# Revit family: Geryon SRD-E01
name_source: partatom
category: Türen
revit_build: Autodesk Revit 2016 (Build: 20150220_1215(x64)
units: mm (PartAtom-declared; Revit-internal decimal feet)

## family parameters
Beim Laden mit Abzugskörper schneiden = Nein
Gemeinsam genutzt = Nein
Immer vertikal = Ja
OmniClass-Nummer = 23.30.10.00
OmniClass-Titel = Doors
Raumberechnungspunkt = Nein

## types (8) — shared parameters
Analytische Konstruktion = <Keine Auswahl>
CoverMaterial = Glas
Date of publishing = 1/16/2017
Design country = Germany
Dicke = 63 mm  [stored 0.206693 ft]
Edition number = 1
ElementWeight = 0.00 kg
FrameMaterial = 1.4401 - A4
Funktion = Außen
HasLockInside = Nein
HasLockInside 120 = Nein
HasLockInside 180 = Nein
HasShellTopFrame = Ja
HasShutOffDevice = Nein
HasShutOffDeviceInside = Nein
HasShutOffDeviceInside120 = Nein
HasShutOffDeviceInside180 = Nein
Hersteller = Kaba GmbH
Konstruktionstyp = Revolving Door
Manufacturer = Kaba GmbH
Manufacturer country = Germany
Manufacturer name = DORMA
Material main = Metal
Material secondary = Glass
Modell = Talos RDR-E01
Nominal height = 2300
OperatingWeight = 0.00 kg
Product SKU = Geryon_SRD-E01
RubberMaterial = Zellkautschuk - EPDM
SectionWidth = 4300 mm
Technical description = http://www.kaba.com
Type = Geryon SRD-E01
URL = http://www.kaba.com
Weight = 0.00 kg
zero-valued in all types: Nominal width

## per-type parameters (varying)
- SRD-E01 1500: AccessLengthOrRadius=780 mm; BaseType=139; ClearHeight=2700 mm; ConsoleS1=831 mm; ConsoleS2=831 mm; ConsoleType=console : Type 5; CoverWidth=200 mm  [stored 0.656168 ft]; Diameter=810 mm; DiameterCoverFront=890 mm  [stored 2.91995 ft]; DiameterGlassInside=789 mm; DiameterGlassOutside=801 mm; DiameterNightLock=840 mm  [stored 2.75591 ft]; DiameterNightLockCover=870 mm; DiameterNightLockFrame=831 mm; DiameterNightLockGlassInside=849 mm  [stored 2.78543 ft]; DiameterNightLockGlassOutside=860 mm; DoorThickness=40 mm  [stored 0.131234 ft]; DoorWidth=740 mm; FrameThickness=63 mm  [stored 0.206693 ft]; FrameThicknessCenter=75 mm; GasShellTopFrame 120=Nein; HandleMaterial=1.4401 - A4; HasCentralColumn=Ja; HasCentralColumn 120=Nein; HasCentralColumn 180=Ja; HasConsoleS1=Ja; HasConsoleS1 120=Nein; HasConsoleS1 180=Ja; HasConsoleS2=Ja; HasConsoleS2 120=Nein; HasConsoleS2 180=Ja; HasGrabHandles=Nein; HasGrabHandles 120=Nein; HasGrabHandles 180=Ja; HasHandleBar=Ja; HasLock=Nein; HasLock 120=Nein; HasLock 180=Nein; HasShellTopFrame 180=Ja; Height=2900 mm; MotorDriveType=K8-SA2; OuterDiameter=2000 mm; ProfileCenter=0 mm  [stored 0 ft]; ProfileWidth=40 mm  [stored 0.131234 ft]; RotationInterval 120=Nein; RotationInterval 180=Ja; StandardUsed=3; Width=1600 mm
- SRD-E01 1700: AccessLengthOrRadius=880 mm; BaseType=109 mm; ClearHeight=2600 mm; ConsoleS1=931 mm; ConsoleS2=931 mm; ConsoleType=console : Type 4; CoverWidth=300 mm; Diameter=910 mm  [stored 2.98556 ft]; DiameterCoverFront=990 mm  [stored 3.24803 ft]; DiameterGlassInside=889 mm; DiameterGlassOutside=901 mm; DiameterNightLock=940 mm; DiameterNightLockCover=970 mm; DiameterNightLockFrame=931 mm; DiameterNightLockGlassInside=949 mm  [stored 3.11352 ft]; DiameterNightLockGlassOutside=960 mm; DoorThickness=25 mm  [stored 0.082021 ft]; DoorWidth=840 mm  [stored 2.75591 ft]; FrameThickness=35 mm  [stored 0.114829 ft]; FrameThicknessCenter=47 mm; GasShellTopFrame 120=Ja; HandleMaterial=1.4401 - A4; HasCentralColumn=Nein; HasCentralColumn 120=Nein; HasCentralColumn 180=Nein; HasConsoleS1=Ja; HasConsoleS1 120=Ja; HasConsoleS1 180=Nein; HasConsoleS2=Ja; HasConsoleS2 120=Ja; HasConsoleS2 180=Nein; HasGrabHandles=Ja; HasGrabHandles 120=Ja; HasGrabHandles 180=Nein; HasHandleBar=Nein; HasLock=Nein; HasLock 120=Nein; HasLock 180=Nein; HasShellTopFrame 180=Nein; Height=2900 mm; MotorDriveType=K8-SA1; OuterDiameter=1800 mm; ProfileCenter=7.5 mm; ProfileWidth=40 mm  [stored 0.131234 ft]; RotationInterval 120=Ja; RotationInterval 180=Nein; StandardUsed=2; Width=1800 mm
- SRD-E01 2900: AccessLengthOrRadius=1480 mm; BaseType=150; ClearHeight=2100 mm; ConsoleS1=1531 mm; ConsoleS2=1531 mm; ConsoleType=console : Type 4; CoverWidth=200 mm  [stored 0.656168 ft]; Diameter=1510 mm; DiameterCoverFront=1590 mm; DiameterGlassInside=1489 mm; DiameterGlassOutside=1501 mm; DiameterNightLock=1540 mm; DiameterNightLockCover=1570 mm; DiameterNightLockFrame=1531 mm; DiameterNightLockGlassInside=1549 mm; DiameterNightLockGlassOutside=1560 mm; DoorThickness=56 mm  [stored 0.183727 ft]; DoorWidth=1440 mm; FrameThickness=80 mm  [stored 0.262467 ft]; FrameThicknessCenter=92 mm  [stored 0.301837 ft]; GasShellTopFrame 120=Nein; HandleMaterial=1.4401 - A4; HasCentralColumn=Nein; HasCentralColumn 120=Nein; HasCentralColumn 180=Nein; HasConsoleS1=Nein; HasConsoleS1 120=Nein; HasConsoleS1 180=Nein; HasConsoleS2=Nein; HasConsoleS2 120=Nein; HasConsoleS2 180=Nein; HasGrabHandles=Nein; HasGrabHandles 120=Nein; HasGrabHandles 180=Ja; HasHandleBar=Ja; HasLock=Nein; HasLock 120=Nein; HasLock 180=Nein; HasShellTopFrame 180=Ja; Height=2300 mm; OuterDiameter=3000 mm; ProfileCenter=0 mm  [stored 0 ft]; ProfileWidth=56 mm  [stored 0.183727 ft]; RotationInterval 120=Nein; RotationInterval 180=Ja; StandardUsed=8; Width=3000 mm
- SRD-E01 1900: AccessLengthOrRadius=980 mm; BaseType=139; ClearHeight=2700 mm; ConsoleS1=1031 mm; ConsoleS2=1031 mm; ConsoleType=console : Type 5; CoverWidth=200 mm  [stored 0.656168 ft]; Diameter=1010 mm; DiameterCoverFront=1090 mm; DiameterGlassInside=989 mm; DiameterGlassOutside=1001 mm; DiameterNightLock=1040 mm; DiameterNightLockCover=1070 mm; DiameterNightLockFrame=1031 mm; DiameterNightLockGlassInside=1049 mm; DiameterNightLockGlassOutside=1060 mm; DoorThickness=40 mm  [stored 0.131234 ft]; DoorWidth=940 mm; FrameThickness=63 mm  [stored 0.206693 ft]; FrameThicknessCenter=75 mm; GasShellTopFrame 120=Nein; HandleMaterial=1.4401 - A4; HasCentralColumn=Ja; HasCentralColumn 120=Nein; HasCentralColumn 180=Ja; HasConsoleS1=Ja; HasConsoleS1 120=Nein; HasConsoleS1 180=Ja; HasConsoleS2=Ja; HasConsoleS2 120=Nein; HasConsoleS2 180=Ja; HasGrabHandles=Nein; HasGrabHandles 120=Nein; HasGrabHandles 180=Ja; HasHandleBar=Ja; HasLock=Nein; HasLock 120=Nein; HasLock 180=Nein; HasShellTopFrame 180=Ja; Height=2900 mm; MotorDriveType=K8-SA2; OuterDiameter=2000 mm; ProfileCenter=0 mm  [stored 0 ft]; ProfileWidth=40 mm  [stored 0.131234 ft]; RotationInterval 120=Nein; RotationInterval 180=Ja; StandardUsed=3; Width=2000 mm
- SRD-E01 2100: AccessLengthOrRadius=1080 mm; BaseType=220; ClearHeight=2400 mm; ConsoleS1=1131 mm; ConsoleS2=1131 mm; ConsoleType=console : Type 5; CoverWidth=300 mm; Diameter=1110 mm; DiameterCoverFront=1190 mm; DiameterGlassInside=1089 mm; DiameterGlassOutside=1101 mm; DiameterNightLock=1140 mm; DiameterNightLockCover=1170 mm; DiameterNightLockFrame=1131 mm; DiameterNightLockGlassInside=1149 mm; DiameterNightLockGlassOutside=1160 mm; DoorThickness=25 mm  [stored 0.082021 ft]; DoorWidth=1040 mm; FrameThickness=49 mm  [stored 0.160761 ft]; FrameThicknessCenter=61 mm; GasShellTopFrame 120=Nein; HandleMaterial=1.4401 - A4; HasCentralColumn=Ja; HasCentralColumn 120=Nein; HasCentralColumn 180=Ja; HasConsoleS1=Nein; HasConsoleS1 120=Nein; HasConsoleS1 180=Nein; HasConsoleS2=Nein; HasConsoleS2 120=Nein; HasConsoleS2 180=Nein; HasGrabHandles=Nein; HasGrabHandles 120=Nein; HasGrabHandles 180=Ja; HasHandleBar=Ja; HasLock=Nein; HasLock 120=Nein; HasLock 180=Nein; HasShellTopFrame 180=Ja; Height=2700 mm; MotorDriveType=K8-SA1; OuterDiameter=2200 mm; ProfileCenter=7.5 mm; ProfileWidth=40 mm  [stored 0.131234 ft]; RotationInterval 120=Nein; RotationInterval 180=Ja; StandardUsed=4; Width=2200 mm
- SRD-E01 2300: AccessLengthOrRadius=1180 mm; BaseType=220; ClearHeight=2100 mm; ConsoleS1=1231 mm; ConsoleS2=1279 mm; ConsoleType=console : Type 5; CoverWidth=200 mm  [stored 0.656168 ft]; Diameter=1210 mm; DiameterCoverFront=1290 mm; DiameterGlassInside=1189 mm; DiameterGlassOutside=1201 mm; DiameterNightLock=1240 mm; DiameterNightLockCover=1270 mm; DiameterNightLockFrame=1231 mm; DiameterNightLockGlassInside=1249 mm; DiameterNightLockGlassOutside=1260 mm; DoorThickness=40 mm  [stored 0.131234 ft]; DoorWidth=1140 mm; FrameThickness=63 mm  [stored 0.206693 ft]; FrameThicknessCenter=75 mm; GasShellTopFrame 120=Nein; HandleMaterial=PA6.6 Gf30(schwarz); HasCentralColumn=Ja; HasCentralColumn 120=Nein; HasCentralColumn 180=Ja; HasConsoleS1=Nein; HasConsoleS1 120=Nein; HasConsoleS1 180=Nein; HasConsoleS2=Nein; HasConsoleS2 120=Nein; HasConsoleS2 180=Nein; HasGrabHandles=Ja; HasGrabHandles 120=Nein; HasGrabHandles 180=Ja; HasHandleBar=Nein; HasLock=Ja; HasLock 120=Nein; HasLock 180=Ja; HasShellTopFrame 180=Ja; Height=2300 mm; MotorDriveType=K8-SA1; OuterDiameter=2400 mm; ProfileCenter=0 mm  [stored 0 ft]; ProfileWidth=40 mm  [stored 0.131234 ft]; RotationInterval 120=Nein; RotationInterval 180=Ja; StandardUsed=5; Width=2400 mm
- SRD-E01 2500: AccessLengthOrRadius=1280 mm; BaseType=170; ClearHeight=2700 mm; ConsoleS1=1331 mm; ConsoleS2=1379 mm; ConsoleType=console : Type 5; CoverWidth=100 mm  [stored 0.328084 ft]; Diameter=1310 mm; DiameterCoverFront=1390 mm; DiameterGlassInside=1289 mm; DiameterGlassOutside=1301 mm; DiameterNightLock=1340 mm; DiameterNightLockCover=1370 mm; DiameterNightLockFrame=1331 mm; DiameterNightLockGlassInside=1349 mm; DiameterNightLockGlassOutside=1360 mm; DoorThickness=25 mm  [stored 0.082021 ft]; DoorWidth=1240 mm; FrameThickness=49 mm  [stored 0.160761 ft]; FrameThicknessCenter=61 mm; GasShellTopFrame 120=Ja; HandleMaterial=PA6.6 Gf30(schwarz); HasCentralColumn=Ja; HasCentralColumn 120=Ja; HasCentralColumn 180=Nein; HasConsoleS1=Ja; HasConsoleS1 120=Ja; HasConsoleS1 180=Nein; HasConsoleS2=Ja; HasConsoleS2 120=Ja; HasConsoleS2 180=Nein; HasGrabHandles=Ja; HasGrabHandles 120=Ja; HasGrabHandles 180=Nein; HasHandleBar=Nein; HasLock=Ja; HasLock 120=Ja; HasLock 180=Nein; HasShellTopFrame 180=Nein; Height=2800 mm; MotorDriveType=K8-SA2; OuterDiameter=2600 mm; ProfileCenter=7.5 mm; ProfileWidth=40 mm  [stored 0.131234 ft]; RotationInterval 120=Ja; RotationInterval 180=Nein; StandardUsed=6; Width=2600 mm
- SRD-E01 2700: AccessLengthOrRadius=1380 mm; BaseType=250; ClearHeight=2800 mm; ConsoleS1=1431 mm; ConsoleS2=1431 mm; ConsoleType=console : Type 4; CoverWidth=300 mm; Diameter=1410 mm; DiameterCoverFront=1490 mm; DiameterGlassInside=1389 mm; DiameterGlassOutside=1401 mm; DiameterNightLock=1440 mm; DiameterNightLockCover=1470 mm; DiameterNightLockFrame=1431 mm; DiameterNightLockGlassInside=1449 mm; DiameterNightLockGlassOutside=1460 mm; DoorThickness=56 mm  [stored 0.183727 ft]; DoorWidth=1340 mm; FrameThickness=80 mm  [stored 0.262467 ft]; FrameThicknessCenter=92 mm  [stored 0.301837 ft]; GasShellTopFrame 120=Ja; HandleMaterial=1.4401 - A4; HasCentralColumn=Ja; HasCentralColumn 120=Ja; HasCentralColumn 180=Nein; HasConsoleS1=Ja; HasConsoleS1 120=Ja; HasConsoleS1 180=Nein; HasConsoleS2=Ja; HasConsoleS2 120=Ja; HasConsoleS2 180=Nein; HasGrabHandles=Nein; HasGrabHandles 120=Ja; HasGrabHandles 180=Nein; HasHandleBar=Ja; HasLock=Nein; HasLock 120=Nein; HasLock 180=Nein; HasShellTopFrame 180=Nein; Height=3100 mm; OuterDiameter=2800 mm; ProfileCenter=0 mm  [stored 0 ft]; ProfileWidth=56 mm  [stored 0.183727 ft]; RotationInterval 120=Ja; RotationInterval 180=Nein; StandardUsed=7; Width=2800 mm

note: [stored X ft] marks values corroborated as IEEE doubles in the binary element streams (Revit-internal decimal feet)
